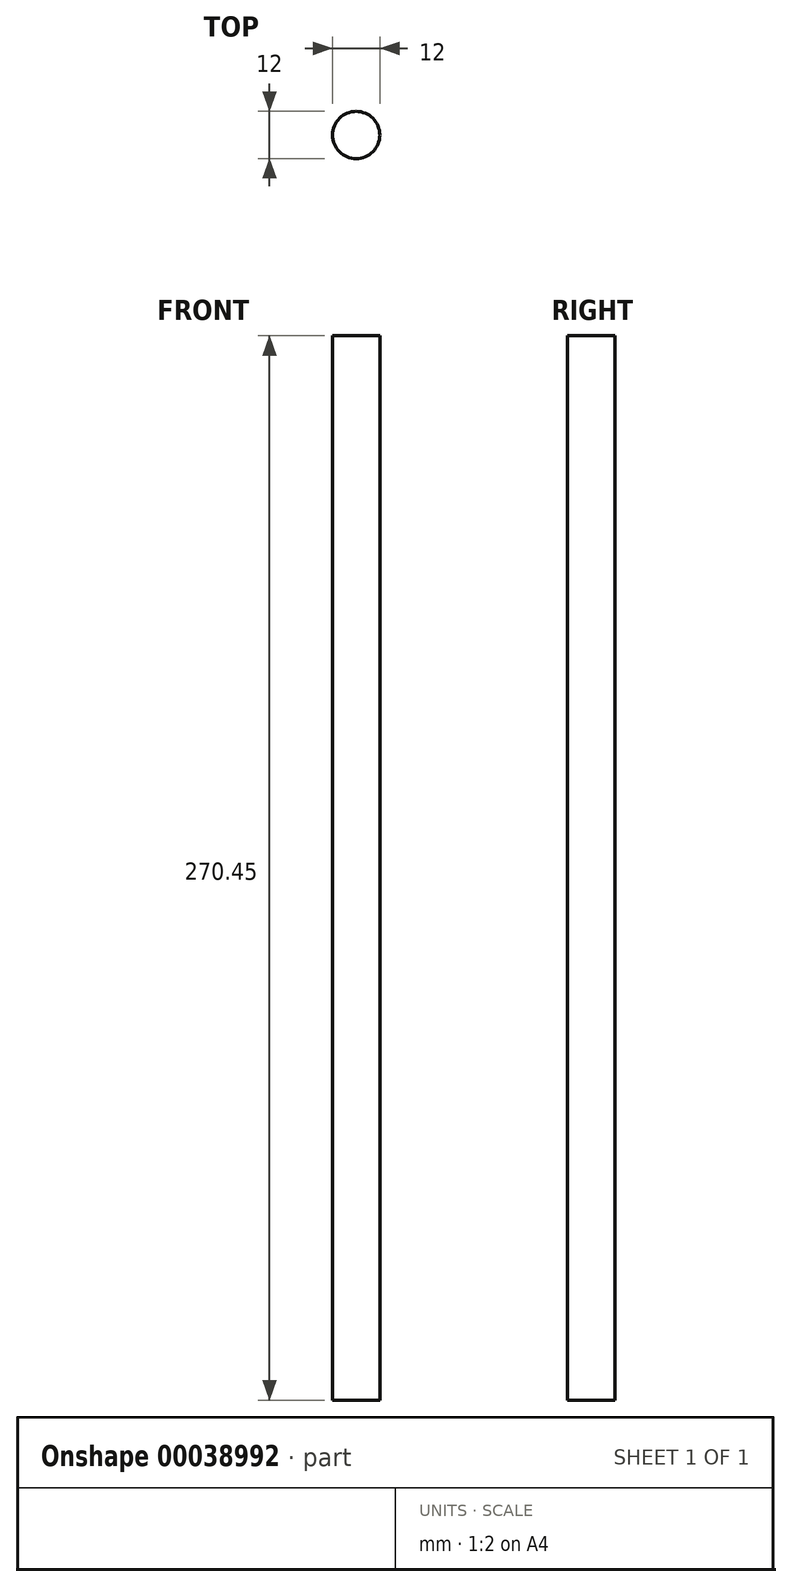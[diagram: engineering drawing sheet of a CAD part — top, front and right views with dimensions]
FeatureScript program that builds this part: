
annotation { "Feature Type Name" : "Feature", "Feature Type Description" : "" }
export const myFeature = defineFeature(function(context is Context, id is Id, definition is map)
    precondition{}
    {
        {
            var Q0;
            Q0=qCreatedBy(makeId("Top.planeOp"),FACE);
            var sketch = newSketch(context, id + "F0", { "sketchPlane" : qUnion([Q0])});
            skCircle(sketch, "E0", {"center": v(0, 0) * mm, "radius": 6 * mm});
            skSolve(sketch);
        }
        {
            var Q0;
            Q0 = qSketchRegion(id + "F0", true);
            extrude(context, id + "F1", {"entities" : qUnion([Q0]), "depth" : 270.45 * mm});
        }
    });
